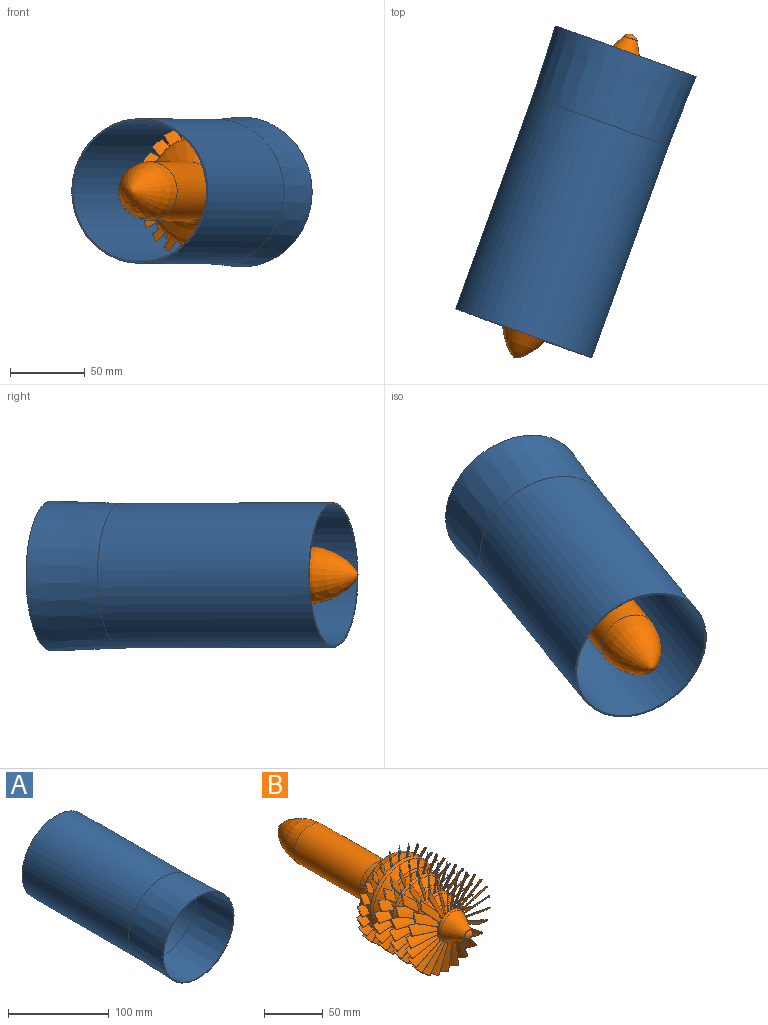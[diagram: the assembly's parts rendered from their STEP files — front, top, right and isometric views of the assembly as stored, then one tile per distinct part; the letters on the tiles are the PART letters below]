
ASSEMBLY  parts=2 mates=1
PART A: 6 faces, bbox 100x200x100 mm
  f0: cone r=50mm half-angle=2deg, axis (0,-1,0), area 15443.1mm2, adj f1,f5
  f1: plane 100x100mm, normal (0,-1,0), area 311mm2, adj f0,f2
  f2: cone r=49mm half-angle=2deg, axis (0,-1,0), area 15128.8mm2, adj f1,f3
  f3: cylinder r=47.25mm len=150mm, axis (0,-1,0), area 44535.8mm2, adj f2,f4
  f4: plane 96.51x96.51mm, normal (0,1,0), area 300mm2, adj f3,f5
  f5: cylinder r=48.25mm len=150mm, axis (0,-1,0), area 45478.3mm2, adj f0,f4
PART B: 370 faces, bbox 95.2x229.3x95.1 mm
  f0: cylinder r=22.77mm len=10.61mm, axis (0,-1,0), area 35.7mm2, adj f178,f180,f367,f369
  f1: cylinder r=22.77mm len=11.53mm, axis (0,-1,0), area 35.7mm2, adj f181,f183,f367,f369
  f2: cylinder r=22.77mm len=11.73mm, axis (0,-1,0), area 30.5mm2, adj f184,f186,f367,f368,f369
  f3: cylinder r=22.77mm len=11.19mm, axis (0,-1,0), area 35.7mm2, adj f187,f189,f367,f369
  f4: cylinder r=22.77mm len=9.95mm, axis (0,-1,0), area 35.7mm2, adj f190,f192,f367,f369
  f5: cylinder r=22.77mm len=8.53mm, axis (0,-1,0), area 35.7mm2, adj f193,f195,f367,f369
  f6: cylinder r=22.77mm len=10.27mm, axis (0,-1,0), area 35.7mm2, adj f196,f198,f367,f369
  f7: cylinder r=22.77mm len=11.37mm, axis (0,-1,0), area 35.7mm2, adj f199,f201,f367,f369
  f8: cylinder r=22.77mm len=11.75mm, axis (0,-1,0), area 35.7mm2, adj f202,f204,f367,f369
  f9: cylinder r=22.77mm len=11.39mm, axis (0,-1,0), area 35.7mm2, adj f205,f207,f367,f369
  f10: cylinder r=22.77mm len=10.32mm, axis (0,-1,0), area 35.7mm2, adj f208,f210,f367,f369
  f11: cylinder r=22.77mm len=8.6mm, axis (0,-1,0), area 35.7mm2, adj f142,f209,f367,f369
  f12: cylinder r=22.77mm len=9.9mm, axis (0,-1,0), area 35.7mm2, adj f139,f141,f367,f369
  f13: cylinder r=22.77mm len=11.16mm, axis (0,-1,0), area 35.7mm2, adj f138,f147,f367,f369
  f14: cylinder r=22.77mm len=11.72mm, axis (0,-1,0), area 30.5mm2, adj f148,f150,f367,f369
  f15: cylinder r=22.77mm len=11.55mm, axis (0,-1,0), area 35.7mm2, adj f145,f151,f367,f369
  f16: cylinder r=22.77mm len=10.65mm, axis (0,-1,0), area 35.7mm2, adj f144,f159,f367,f369
  f17: cylinder r=22.77mm len=9.08mm, axis (0,-1,0), area 35.7mm2, adj f160,f162,f367,f369
  f18: cylinder r=22.77mm len=9.48mm, axis (0,-1,0), area 35.7mm2, adj f157,f163,f367,f369
  f19: cylinder r=22.77mm len=10.91mm, axis (0,-1,0), area 35.7mm2, adj f154,f156,f367,f369
  f20: cylinder r=22.77mm len=11.65mm, axis (0,-1,0), area 35.7mm2, adj f153,f166,f367,f369
  f21: cylinder r=22.77mm len=11.66mm, axis (0,-1,0), area 35.7mm2, adj f165,f169,f367,f369
  f22: cylinder r=22.77mm len=10.94mm, axis (0,-1,0), area 35.7mm2, adj f168,f172,f367,f369
  f23: cylinder r=22.77mm len=9.53mm, axis (0,-1,0), area 35.7mm2, adj f171,f175,f367,f369
  f24: cylinder r=30.05mm len=12.66mm, axis (0,-1,0), area 48mm2, adj f328,f330,f365,f366
  f25: cylinder r=30.05mm len=13.49mm, axis (0,-1,0), area 48mm2, adj f331,f333,f365,f366
  f26: cylinder r=30.05mm len=13.47mm, axis (0,-1,0), area 48mm2, adj f334,f336,f365,f366
  f27: cylinder r=30.05mm len=12.6mm, axis (0,-1,0), area 48mm2, adj f337,f339,f365,f366
  f28: cylinder r=30.05mm len=10.95mm, axis (0,-1,0), area 48mm2, adj f340,f342,f365,f366
  f29: cylinder r=30.05mm len=10.52mm, axis (0,-1,0), area 48mm2, adj f343,f345,f365,f366
  f30: cylinder r=30.05mm len=12.33mm, axis (0,-1,0), area 48mm2, adj f346,f348,f365,f366
  f31: cylinder r=30.05mm len=13.36mm, axis (0,-1,0), area 48mm2, adj f349,f351,f365,f366
  f32: cylinder r=30.05mm len=13.55mm, axis (0,-1,0), area 48mm2, adj f352,f354,f365,f366
  f33: cylinder r=30.05mm len=12.9mm, axis (0,-1,0), area 48mm2, adj f355,f357,f365,f366
  f34: cylinder r=30.05mm len=11.43mm, axis (0,-1,0), area 48mm2, adj f358,f360,f365,f366
  f35: cylinder r=30.05mm len=9.96mm, axis (0,-1,0), area 48mm2, adj f291,f359,f365,f366
  f36: cylinder r=30.05mm len=11.94mm, axis (0,-1,0), area 48mm2, adj f288,f292,f365,f366
  f37: cylinder r=30.05mm len=13.18mm, axis (0,-1,0), area 48mm2, adj f289,f297,f365,f366
  f38: cylinder r=30.05mm len=13.59mm, axis (0,-1,0), area 48mm2, adj f298,f300,f365,f366
  f39: cylinder r=30.05mm len=13.14mm, axis (0,-1,0), area 48mm2, adj f294,f301,f365,f366
  f40: cylinder r=30.05mm len=11.87mm, axis (0,-1,0), area 48mm2, adj f295,f309,f365,f366
  f41: cylinder r=30.05mm len=9.85mm, axis (0,-1,0), area 48mm2, adj f310,f312,f365,f366
  f42: cylinder r=30.05mm len=11.51mm, axis (0,-1,0), area 48mm2, adj f306,f313,f365,f366
  f43: cylinder r=30.05mm len=12.95mm, axis (0,-1,0), area 48mm2, adj f303,f307,f365,f366
  f44: cylinder r=30.05mm len=13.56mm, axis (0,-1,0), area 48mm2, adj f304,f316,f365,f366
  f45: cylinder r=30.05mm len=13.33mm, axis (0,-1,0), area 48mm2, adj f315,f319,f365,f366
  f46: cylinder r=30.05mm len=12.26mm, axis (0,-1,0), area 48mm2, adj f318,f322,f365,f366
  f47: cylinder r=30.05mm len=10.42mm, axis (0,-1,0), area 48mm2, adj f321,f325,f365,f366
  f48: cylinder r=30.05mm len=11.04mm, axis (0,-1,0), area 48mm2, adj f324,f327,f365,f366
  f49: cylinder r=37.33mm len=74.66mm, axis (0,-1,0), area 1745mm2, adj f50,f59,f213,f214,f216,f217,f219,f220
  f50: cylinder r=37.33mm len=6.36mm, axis (0,-1,0), area 18.9mm2, adj f49,f258,f364
  f51: cylinder r=22.77mm len=9.02mm, axis (0,-1,0), area 35.7mm2, adj f174,f177,f367,f369
  f52: cylinder r=15.49mm len=30.98mm, axis (0,-1,0), area 575mm2, adj f53,f63,f64,f66,f67,f69,f70,f72
  f53: cylinder r=15.49mm len=3.79mm, axis (0,-1,0), area 6.1mm2, adj f52,f96,f100,f362
  f54: cone r=22.77mm half-angle=36.1deg, axis (0,1,0), area 1095.6mm2, adj f362,f369
  f55: cone r=15.49mm half-angle=28.8deg, axis (0,1,0), area 1297.2mm2, adj f56,f363
  f56: sphere r=5.39mm, area 94.4mm2, adj f55
  f57: revolved ~39.03x38.98mm, area 3530.5mm2, adj f58
  f58: cylinder r=19.54mm len=78.57mm, axis (0,-1,0), area 9647.2mm2, adj f57,f59
  f59: revolved ~74.66x74.66mm, area 5313.1mm2, adj f49,f58
  f60: cone r=37.33mm half-angle=36.1deg, axis (0,1,0), area 1929.3mm2, adj f364,f365
  f61: cone r=30.05mm half-angle=36.1deg, axis (0,1,0), area 1512.5mm2, adj f366,f367
  f62: cone r=49mm half-angle=2deg, axis (0,-1,0), area 4.1mm2, adj f63,f64
  f63: extruded ~33.09x14.94mm, area 321.3mm2, adj f52,f62,f64,f362
  f64: extruded ~33.12x14.9mm, area 321.3mm2, adj f52,f62,f63,f362
  f65: cone r=49mm half-angle=2deg, axis (0,-1,0), area 4.1mm2, adj f66,f67
  f66: extruded ~31.77x21.82mm, area 321.3mm2, adj f52,f65,f67,f362
  f67: extruded ~31.78x21.8mm, area 321.3mm2, adj f52,f65,f66,f362
  f68: cone r=49mm half-angle=2deg, axis (0,-1,0), area 4.1mm2, adj f69,f70
  f69: extruded ~28.45x27.33mm, area 321.3mm2, adj f52,f68,f70,f362
  f70: extruded ~28.45x27.32mm, area 321.3mm2, adj f52,f68,f69,f362
  f71: cone r=49mm half-angle=2deg, axis (0,-1,0), area 4.1mm2, adj f72,f73
  f72: extruded ~31.12x23.34mm, area 321.3mm2, adj f52,f71,f73,f362
  f73: extruded ~31.13x23.32mm, area 321.3mm2, adj f52,f71,f72,f362
  f74: cone r=49mm half-angle=2deg, axis (0,-1,0), area 4.1mm2, adj f75,f76
  f75: extruded ~32.96x16.76mm, area 321.3mm2, adj f52,f74,f76,f362
  f76: extruded ~32.98x16.73mm, area 321.3mm2, adj f52,f74,f75,f362
  f77: cone r=49mm half-angle=2deg, axis (0,-1,0), area 4.1mm2, adj f78,f79
  f78: extruded ~32.72x9.13mm, area 321.3mm2, adj f52,f77,f79,f362
  f79: extruded ~32.76x9.09mm, area 321.3mm2, adj f52,f77,f78,f362
  f80: cone r=49mm half-angle=2deg, axis (0,-1,0), area 4.1mm2, adj f81,f82
  f81: extruded ~33.1x13.05mm, area 321.3mm2, adj f52,f80,f82,f362
  f82: extruded ~33.13x13.01mm, area 321.3mm2, adj f52,f80,f81,f362
  f83: cone r=49mm half-angle=2deg, axis (0,-1,0), area 4.1mm2, adj f84,f85
  f84: extruded ~32.29x20.21mm, area 321.3mm2, adj f52,f83,f85,f362
  f85: extruded ~32.31x20.19mm, area 321.3mm2, adj f52,f83,f84,f362
  f86: cone r=49mm half-angle=2deg, axis (0,-1,0), area 4.1mm2, adj f87,f88
  f87: extruded ~29.45x26.1mm, area 321.3mm2, adj f52,f86,f88,f362
  f88: extruded ~29.46x26.09mm, area 321.3mm2, adj f52,f86,f87,f362
  f89: cone r=49mm half-angle=2deg, axis (0,-1,0), area 4.1mm2, adj f90,f91
  f90: extruded ~30.35x24.77mm, area 321.3mm2, adj f52,f89,f91,f362
  f91: extruded ~30.35x24.76mm, area 321.3mm2, adj f52,f89,f90,f362
  f92: cone r=49mm half-angle=2deg, axis (0,-1,0), area 4.1mm2, adj f93,f94
  f93: extruded ~32.69x18.52mm, area 321.3mm2, adj f52,f92,f94,f362
  f94: extruded ~32.71x18.5mm, area 321.3mm2, adj f52,f92,f93,f362
  f95: cone r=49mm half-angle=2deg, axis (0,-1,0), area 4.1mm2, adj f96,f97
  f96: extruded ~32.97x11.11mm, area 321.7mm2, adj f52,f53,f95,f97,f362
  f97: extruded ~33.01x11.07mm, area 321.3mm2, adj f52,f95,f96,f362
  f98: cone r=49mm half-angle=2deg, axis (0,-1,0), area 4.1mm2, adj f99,f100
  f99: extruded ~32.98x11.11mm, area 321.3mm2, adj f52,f98,f100,f362
  f100: extruded ~33.01x11.07mm, area 321.3mm2, adj f52,f53,f98,f99,f362
  f101: cone r=49mm half-angle=2deg, axis (0,-1,0), area 4.1mm2, adj f102,f103
  f102: extruded ~32.71x18.5mm, area 321.3mm2, adj f52,f101,f103,f362
  f103: extruded ~32.69x18.52mm, area 321.3mm2, adj f52,f101,f102,f362
  f104: cone r=49mm half-angle=2deg, axis (0,-1,0), area 4.1mm2, adj f105,f106
  f105: extruded ~30.35x24.76mm, area 321.3mm2, adj f52,f104,f106,f362
  f106: extruded ~30.35x24.77mm, area 321.3mm2, adj f52,f104,f105,f362
  f107: cone r=49mm half-angle=2deg, axis (0,-1,0), area 4.1mm2, adj f108,f109
  f108: extruded ~29.46x26.09mm, area 321.3mm2, adj f52,f107,f109,f362
  f109: extruded ~29.45x26.1mm, area 321.3mm2, adj f52,f107,f108,f362
  f110: cone r=49mm half-angle=2deg, axis (0,-1,0), area 4.1mm2, adj f111,f112
  f111: extruded ~32.31x20.19mm, area 321.3mm2, adj f52,f110,f112,f362
  f112: extruded ~32.29x20.21mm, area 321.3mm2, adj f52,f110,f111,f362
  f113: cone r=49mm half-angle=2deg, axis (0,-1,0), area 4.1mm2, adj f114,f115
  f114: extruded ~33.13x13.01mm, area 321.3mm2, adj f52,f113,f115,f362
  f115: extruded ~33.1x13.05mm, area 321.3mm2, adj f52,f113,f114,f362
  f116: cone r=49mm half-angle=2deg, axis (0,-1,0), area 4.1mm2, adj f117,f118
  f117: extruded ~32.76x9.09mm, area 321.3mm2, adj f52,f116,f118,f362
  f118: extruded ~32.72x9.13mm, area 321.3mm2, adj f52,f116,f117,f362
  f119: cone r=49mm half-angle=2deg, axis (0,-1,0), area 4.1mm2, adj f120,f121
  f120: extruded ~32.98x16.73mm, area 321.3mm2, adj f52,f119,f121,f362
  f121: extruded ~32.96x16.76mm, area 321.3mm2, adj f52,f119,f120,f362
  f122: cone r=49mm half-angle=2deg, axis (0,-1,0), area 4.1mm2, adj f123,f124
  f123: extruded ~31.13x23.32mm, area 321.3mm2, adj f52,f122,f124,f362
  f124: extruded ~31.12x23.34mm, area 321.3mm2, adj f52,f122,f123,f362
  f125: cone r=49mm half-angle=2deg, axis (0,-1,0), area 4.1mm2, adj f126,f127
  f126: extruded ~28.45x27.32mm, area 321.3mm2, adj f52,f125,f127,f362
  f127: extruded ~28.45x27.33mm, area 321.3mm2, adj f52,f125,f126,f362
  f128: cone r=49mm half-angle=2deg, axis (0,-1,0), area 4.1mm2, adj f129,f130
  f129: extruded ~31.78x21.8mm, area 321.3mm2, adj f52,f128,f130,f362
  f130: extruded ~31.77x21.82mm, area 321.3mm2, adj f52,f128,f129,f362
  f131: cone r=49mm half-angle=2deg, axis (0,-1,0), area 4.1mm2, adj f132,f133
  f132: extruded ~33.12x14.9mm, area 321.3mm2, adj f52,f131,f133,f362
  f133: extruded ~33.09x14.94mm, area 321.3mm2, adj f52,f131,f132,f362
  f134: extruded ~32.34x7.12mm, area 321.3mm2, adj f52,f135,f136,f362
  f135: extruded ~32.38x7.12mm, area 321.3mm2, adj f52,f134,f136,f362
  f136: cone r=49mm half-angle=2deg, axis (0,-1,0), area 4.1mm2, adj f134,f135
  f137: cone r=49mm half-angle=2deg, axis (0,-1,0), area 4.1mm2, adj f138,f139
  f138: extruded ~24.97x16.62mm, area 240.7mm2, adj f13,f137,f139,f367,f369
  f139: extruded ~25x16.6mm, area 240.8mm2, adj f12,f137,f138,f367,f369
  f140: cone r=49mm half-angle=2deg, axis (0,-1,0), area 4.1mm2, adj f141,f142
  f141: extruded ~23.27x20.83mm, area 240.7mm2, adj f12,f140,f142,f367,f369
  f142: extruded ~23.28x20.82mm, area 240.8mm2, adj f11,f140,f141,f367,f369
  f143: cone r=49mm half-angle=2deg, axis (0,-1,0), area 4.1mm2, adj f144,f145
  f144: extruded ~25.23x14.4mm, area 240.7mm2, adj f16,f143,f145,f367,f369
  f145: extruded ~25.27x14.37mm, area 240.8mm2, adj f15,f143,f144,f367,f369
  f146: cone r=49mm half-angle=2deg, axis (0,-1,0), area 4.1mm2, adj f147,f148
  f147: extruded ~25.15x11.34mm, area 240.8mm2, adj f13,f146,f148,f367,f369
  f148: extruded ~25.11x11.37mm, area 240.7mm2, adj f14,f146,f147,f367,f369
  f149: cone r=49mm half-angle=2deg, axis (0,-1,0), area 4.1mm2, adj f150,f151
  f150: extruded ~24.71x8.75mm, area 240.8mm2, adj f14,f149,f151,f367,f369
  f151: extruded ~24.66x8.79mm, area 240.7mm2, adj f15,f149,f150,f367,f369
  f152: cone r=49mm half-angle=2deg, axis (0,-1,0), area 4.1mm2, adj f153,f154
  f153: extruded ~25.22x12.77mm, area 240.7mm2, adj f20,f152,f154,f367,f369
  f154: extruded ~25.26x12.73mm, area 240.8mm2, adj f19,f152,f153,f367,f369
  f155: cone r=49mm half-angle=2deg, axis (0,-1,0), area 4.1mm2, adj f156,f157
  f156: extruded ~24.69x17.78mm, area 240.7mm2, adj f19,f155,f157,f367,f369
  f157: extruded ~24.72x17.77mm, area 240.8mm2, adj f18,f155,f156,f367,f369
  f158: cone r=49mm half-angle=2deg, axis (0,-1,0), area 4.1mm2, adj f159,f160
  f159: extruded ~24.24x19.09mm, area 240.8mm2, adj f16,f158,f160,f367,f369
  f160: extruded ~24.22x19.1mm, area 240.7mm2, adj f17,f158,f159,f367,f369
  f161: cone r=49mm half-angle=2deg, axis (0,-1,0), area 4.1mm2, adj f162,f163
  f162: extruded ~22.62x21.68mm, area 240.8mm2, adj f17,f161,f163,f367,f369
  f163: extruded ~22.61x21.68mm, area 240.7mm2, adj f18,f161,f162,f367,f369
  f164: cone r=49mm half-angle=2deg, axis (0,-1,0), area 4.1mm2, adj f165,f166
  f165: extruded ~24.27x7.29mm, area 240.7mm2, adj f21,f164,f166,f367,f369
  f166: extruded ~24.32x7.24mm, area 240.8mm2, adj f20,f164,f165,f367,f369
  f167: cone r=49mm half-angle=2deg, axis (0,-1,0), area 4.1mm2, adj f168,f169
  f168: extruded ~25.24x13.07mm, area 240.7mm2, adj f22,f167,f169,f367,f369
  f169: extruded ~25.28x13.04mm, area 240.8mm2, adj f21,f167,f168,f367,f369
  f170: cone r=49mm half-angle=2deg, axis (0,-1,0), area 4.1mm2, adj f171,f172
  f171: extruded ~24.62x18.03mm, area 240.7mm2, adj f23,f170,f172,f367,f369
  f172: extruded ~24.64x18.02mm, area 240.8mm2, adj f22,f170,f171,f367,f369
  f173: cone r=49mm half-angle=2deg, axis (0,-1,0), area 4.1mm2, adj f174,f175
  f174: extruded ~22.45x21.86mm, area 240.7mm2, adj f51,f173,f175,f367,f369
  f175: extruded ~22.46x21.86mm, area 240.8mm2, adj f23,f173,f174,f367,f369
  f176: cone r=49mm half-angle=2deg, axis (0,-1,0), area 4.1mm2, adj f177,f178
  f177: extruded ~24.33x18.86mm, area 240.8mm2, adj f51,f176,f178,f367,f369
  f178: extruded ~24.31x18.87mm, area 240.7mm2, adj f0,f176,f177,f367,f369
  f179: cone r=49mm half-angle=2deg, axis (0,-1,0), area 4.1mm2, adj f180,f181
  f180: extruded ~25.28x14.08mm, area 240.8mm2, adj f0,f179,f181,f367,f369
  f181: extruded ~25.24x14.11mm, area 240.7mm2, adj f1,f179,f180,f367,f369
  f182: cone r=49mm half-angle=2deg, axis (0,-1,0), area 4.1mm2, adj f183,f184
  f183: extruded ~24.63x8.42mm, area 240.8mm2, adj f1,f182,f184,f367,f369
  f184: extruded ~24.58x8.46mm, area 240.7mm2, adj f2,f182,f183,f367,f369
  f185: cone r=49mm half-angle=2deg, axis (0,-1,0), area 4.1mm2, adj f186,f187
  f186: extruded ~25.19x11.65mm, area 240.8mm2, adj f2,f185,f187,f368,f369
  f187: extruded ~25.14x11.69mm, area 240.7mm2, adj f3,f185,f186,f367,f369
  f188: cone r=49mm half-angle=2deg, axis (0,-1,0), area 4.1mm2, adj f189,f190
  f189: extruded ~24.95x16.87mm, area 240.8mm2, adj f3,f188,f190,f367,f369
  f190: extruded ~24.92x16.89mm, area 240.7mm2, adj f4,f188,f189,f367,f369
  f191: cone r=49mm half-angle=2deg, axis (0,-1,0), area 4.1mm2, adj f192,f193
  f192: extruded ~23.14x21.02mm, area 240.8mm2, adj f4,f191,f193,f367,f369
  f193: extruded ~23.13x21.02mm, area 240.7mm2, adj f5,f191,f192,f367,f369
  f194: cone r=49mm half-angle=2deg, axis (0,-1,0), area 4.1mm2, adj f195,f196
  f195: extruded ~23.85x19.88mm, area 240.8mm2, adj f5,f194,f196,f367,f369
  f196: extruded ~23.84x19.89mm, area 240.7mm2, adj f6,f194,f195,f367,f369
  f197: cone r=49mm half-angle=2deg, axis (0,-1,0), area 4.1mm2, adj f198,f199
  f198: extruded ~25.19x15.37mm, area 240.8mm2, adj f6,f197,f199,f367,f369
  f199: extruded ~25.16x15.4mm, area 240.7mm2, adj f7,f197,f198,f367,f369
  f200: cone r=49mm half-angle=2deg, axis (0,-1,0), area 4.1mm2, adj f201,f202
  f201: extruded ~24.94x9.9mm, area 240.8mm2, adj f7,f200,f202,f367,f369
  f202: extruded ~24.89x9.94mm, area 240.7mm2, adj f8,f200,f201,f367,f369
  f203: cone r=49mm half-angle=2deg, axis (0,-1,0), area 4.1mm2, adj f204,f205
  f204: extruded ~25x10.22mm, area 240.8mm2, adj f8,f203,f205,f367,f369
  f205: extruded ~24.95x10.26mm, area 240.7mm2, adj f9,f203,f204,f367,f369
  f206: cone r=49mm half-angle=2deg, axis (0,-1,0), area 4.1mm2, adj f207,f208
  f207: extruded ~25.16x15.65mm, area 240.8mm2, adj f9,f206,f208,f367,f369
  f208: extruded ~25.12x15.67mm, area 240.7mm2, adj f10,f206,f207,f367,f369
  f209: extruded ~23.72x20.1mm, area 240.7mm2, adj f11,f210,f211,f367,f369
  f210: extruded ~23.73x20.1mm, area 240.8mm2, adj f10,f209,f211,f367,f369
  f211: cone r=49mm half-angle=2deg, axis (0,-1,0), area 4.1mm2, adj f209,f210
  f212: cylinder r=47.25mm len=7.07mm, axis (0,-1,0), area 4.1mm2, adj f213,f214
  f213: extruded ~10.75x9.4mm, area 90.5mm2, adj f49,f212,f214,f364
  f214: extruded ~10.77x9.44mm, area 89.7mm2, adj f49,f212,f213,f364
  f215: cylinder r=47.25mm len=7.07mm, axis (0,-1,0), area 4.1mm2, adj f216,f217
  f216: extruded ~11.44x10.76mm, area 90.5mm2, adj f49,f215,f217,f364
  f217: extruded ~11.47x10.8mm, area 89.7mm2, adj f49,f215,f216,f364
  f218: cylinder r=47.25mm len=7.12mm, axis (0,-1,0), area 4.1mm2, adj f219,f220
  f219: extruded ~9.38x7.45mm, area 90.5mm2, adj f49,f218,f220,f364
  f220: extruded ~9.39x7.49mm, area 89.7mm2, adj f49,f218,f219,f364
  f221: cylinder r=47.25mm len=7.07mm, axis (0,-1,0), area 4.1mm2, adj f222,f223
  f222: extruded ~10.37x8.81mm, area 90.5mm2, adj f49,f221,f223,f364
  f223: extruded ~10.38x8.85mm, area 89.7mm2, adj f49,f221,f222,f364
  f224: cylinder r=47.25mm len=7.07mm, axis (0,-1,0), area 4.1mm2, adj f225,f226
  f225: extruded ~11.29x10.38mm, area 90.5mm2, adj f49,f224,f226,f364
  f226: extruded ~11.31x10.42mm, area 89.7mm2, adj f49,f224,f225,f364
  f227: cylinder r=47.25mm len=7.09mm, axis (0,-1,0), area 4.1mm2, adj f228,f229
  f228: extruded ~9.79x7.98mm, area 90.5mm2, adj f49,f227,f229,f364
  f229: extruded ~9.79x8.03mm, area 89.7mm2, adj f49,f227,f228,f364
  f230: cylinder r=47.25mm len=7.07mm, axis (0,-1,0), area 4.1mm2, adj f231,f232
  f231: extruded ~10.99x9.8mm, area 90.5mm2, adj f49,f230,f232,f364
  f232: extruded ~11.01x9.84mm, area 89.7mm2, adj f49,f230,f231,f364
  f233: cylinder r=47.25mm len=7.07mm, axis (0,-1,0), area 4.1mm2, adj f234,f235
  f234: extruded ~11.51x11.3mm, area 90.5mm2, adj f49,f233,f235,f364
  f235: extruded ~11.54x11.33mm, area 89.7mm2, adj f49,f233,f234,f364
  f236: cylinder r=47.25mm len=7.07mm, axis (0,-1,0), area 4.1mm2, adj f237,f238
  f237: extruded ~11.5x11mm, area 90.5mm2, adj f49,f236,f238,f364
  f238: extruded ~11.53x11.04mm, area 89.7mm2, adj f49,f236,f237,f364
  f239: cylinder r=47.25mm len=7.07mm, axis (0,-1,0), area 4.1mm2, adj f240,f241
  f240: extruded ~10.04x8.37mm, area 89.7mm2, adj f49,f239,f241,f364
  f241: extruded ~10.03x8.32mm, area 90.5mm2, adj f49,f239,f240,f364
  f242: cylinder r=47.25mm len=7.07mm, axis (0,-1,0), area 4.1mm2, adj f243,f244
  f243: extruded ~11.15x10.09mm, area 89.7mm2, adj f49,f242,f244,f364
  f244: extruded ~11.13x10.04mm, area 90.5mm2, adj f49,f242,f243,f364
  f245: cylinder r=47.25mm len=7.07mm, axis (0,-1,0), area 4.1mm2, adj f246,f247
  f246: extruded ~11.55x11.17mm, area 89.7mm2, adj f49,f245,f247,f364
  f247: extruded ~11.52x11.13mm, area 90.5mm2, adj f49,f245,f246,f364
  f248: cylinder r=47.25mm len=7.07mm, axis (0,-1,0), area 4.1mm2, adj f249,f250
  f249: extruded ~11.55x11.23mm, area 89.7mm2, adj f49,f248,f250,f364
  f250: extruded ~11.52x11.19mm, area 90.5mm2, adj f49,f248,f249,f364
  f251: cylinder r=47.25mm len=7.07mm, axis (0,-1,0), area 4.1mm2, adj f252,f253
  f252: extruded ~11.19x10.16mm, area 90.5mm2, adj f49,f251,f253,f364
  f253: extruded ~11.21x10.2mm, area 89.7mm2, adj f49,f251,f252,f364
  f254: cylinder r=47.25mm len=7.07mm, axis (0,-1,0), area 4.1mm2, adj f255,f256
  f255: extruded ~10.15x8.49mm, area 90.5mm2, adj f49,f254,f256,f364
  f256: extruded ~10.16x8.54mm, area 89.7mm2, adj f49,f254,f255,f364
  f257: cylinder r=47.25mm len=7.1mm, axis (0,-1,0), area 4.1mm2, adj f258,f259
  f258: extruded ~9.66x7.81mm, area 90.4mm2, adj f49,f50,f257,f259,f364
  f259: extruded ~9.66x7.85mm, area 89.7mm2, adj f49,f257,f258,f364
  f260: cylinder r=47.25mm len=7.07mm, axis (0,-1,0), area 4.1mm2, adj f261,f262
  f261: extruded ~10.92x9.67mm, area 90.5mm2, adj f49,f260,f262,f364
  f262: extruded ~10.93x9.71mm, area 89.7mm2, adj f49,f260,f261,f364
  f263: cylinder r=47.25mm len=7.07mm, axis (0,-1,0), area 4.1mm2, adj f264,f265
  f264: extruded ~11.49x10.92mm, area 90.5mm2, adj f49,f263,f265,f364
  f265: extruded ~11.52x10.96mm, area 89.7mm2, adj f49,f263,f264,f364
  f266: cylinder r=47.25mm len=7.07mm, axis (0,-1,0), area 4.1mm2, adj f267,f268
  f267: extruded ~11.49x11.34mm, area 90.5mm2, adj f49,f266,f268,f364
  f268: extruded ~11.52x11.38mm, area 89.7mm2, adj f49,f266,f267,f364
  f269: cylinder r=47.25mm len=7.07mm, axis (0,-1,0), area 4.1mm2, adj f270,f271
  f270: extruded ~11.34x10.48mm, area 90.5mm2, adj f49,f269,f271,f364
  f271: extruded ~11.36x10.52mm, area 89.7mm2, adj f49,f269,f270,f364
  f272: cylinder r=47.25mm len=7.07mm, axis (0,-1,0), area 4.1mm2, adj f273,f274
  f273: extruded ~10.47x8.96mm, area 90.5mm2, adj f49,f272,f274,f364
  f274: extruded ~10.48x9.01mm, area 89.7mm2, adj f49,f272,f273,f364
  f275: cylinder r=47.25mm len=7.13mm, axis (0,-1,0), area 4.1mm2, adj f276,f277
  f276: extruded ~9.24x7.26mm, area 90.5mm2, adj f49,f275,f277,f364
  f277: extruded ~9.25x7.31mm, area 89.7mm2, adj f49,f275,f276,f364
  f278: cylinder r=47.25mm len=7.07mm, axis (0,-1,0), area 4.1mm2, adj f279,f280
  f279: extruded ~10.66x9.26mm, area 90.5mm2, adj f49,f278,f280,f364
  f280: extruded ~10.68x9.3mm, area 89.7mm2, adj f49,f278,f279,f364
  f281: cylinder r=47.25mm len=7.07mm, axis (0,-1,0), area 4.1mm2, adj f282,f283
  f282: extruded ~11.41x10.67mm, area 90.5mm2, adj f49,f281,f283,f364
  f283: extruded ~11.44x10.71mm, area 89.7mm2, adj f49,f281,f282,f364
  f284: extruded ~11.48x11.45mm, area 89.7mm2, adj f49,f285,f286,f364
  f285: extruded ~11.45x11.42mm, area 90.5mm2, adj f49,f284,f286,f364
  f286: cylinder r=47.25mm len=7.07mm, axis (0,-1,0), area 4.1mm2, adj f284,f285
  f287: cylinder r=47.25mm len=7.07mm, axis (0,-1,0), area 4.1mm2, adj f288,f289
  f288: extruded ~17.86x12.44mm, area 162.9mm2, adj f36,f287,f289,f365,f366
  f289: extruded ~17.88x12.48mm, area 162.9mm2, adj f37,f287,f288,f365,f366
  f290: cylinder r=47.25mm len=7.07mm, axis (0,-1,0), area 4.1mm2, adj f291,f292
  f291: extruded ~17.49x15.24mm, area 162.9mm2, adj f35,f290,f292,f365,f366
  f292: extruded ~17.52x15.28mm, area 162.9mm2, adj f36,f290,f291,f365,f366
  f293: cylinder r=47.25mm len=7.07mm, axis (0,-1,0), area 4.1mm2, adj f294,f295
  f294: extruded ~17.87x12.79mm, area 162.9mm2, adj f39,f293,f295,f365,f366
  f295: extruded ~17.89x12.84mm, area 162.9mm2, adj f40,f293,f294,f365,f366
  f296: cylinder r=47.25mm len=7.09mm, axis (0,-1,0), area 4.1mm2, adj f297,f298
  f297: extruded ~17.1x8.86mm, area 162.9mm2, adj f37,f296,f298,f365,f366
  f298: extruded ~17.11x8.9mm, area 162.9mm2, adj f38,f296,f297,f365,f366
  f299: cylinder r=47.25mm len=7.07mm, axis (0,-1,0), area 4.1mm2, adj f300,f301
  f300: extruded ~17.24x9.29mm, area 162.9mm2, adj f38,f299,f301,f365,f366
  f301: extruded ~17.25x9.33mm, area 162.9mm2, adj f39,f299,f300,f365,f366
  f302: cylinder r=47.25mm len=7.07mm, axis (0,-1,0), area 4.1mm2, adj f303,f304
  f303: extruded ~17.39x9.81mm, area 162.9mm2, adj f43,f302,f304,f365,f366
  f304: extruded ~17.41x9.86mm, area 162.9mm2, adj f44,f302,f303,f365,f366
  f305: cylinder r=47.25mm len=7.07mm, axis (0,-1,0), area 4.1mm2, adj f306,f307
  f306: extruded ~17.87x13.22mm, area 162.9mm2, adj f42,f305,f307,f365,f366
  f307: extruded ~17.89x13.27mm, area 162.9mm2, adj f43,f305,f306,f365,f366
  f308: cylinder r=47.25mm len=7.07mm, axis (0,-1,0), area 4.1mm2, adj f309,f310
  f309: extruded ~17.38x15.5mm, area 162.9mm2, adj f40,f308,f310,f365,f366
  f310: extruded ~17.41x15.54mm, area 162.9mm2, adj f41,f308,f309,f365,f366
  f311: cylinder r=47.25mm len=7.07mm, axis (0,-1,0), area 4.1mm2, adj f312,f313
  f312: extruded ~17.22x15.8mm, area 162.9mm2, adj f41,f311,f313,f365,f366
  f313: extruded ~17.26x15.84mm, area 162.9mm2, adj f42,f311,f312,f365,f366
  f314: cylinder r=47.25mm len=7.11mm, axis (0,-1,0), area 4.1mm2, adj f315,f316
  f315: extruded ~16.92x8.36mm, area 162.9mm2, adj f45,f314,f316,f365,f366
  f316: extruded ~16.91x8.31mm, area 162.9mm2, adj f44,f314,f315,f365,f366
  f317: cylinder r=47.25mm len=7.07mm, axis (0,-1,0), area 4.1mm2, adj f318,f319
  f318: extruded ~17.84x12.03mm, area 162.9mm2, adj f46,f317,f319,f365,f366
  f319: extruded ~17.82x11.98mm, area 162.9mm2, adj f45,f317,f318,f365,f366
  f320: cylinder r=47.25mm len=7.07mm, axis (0,-1,0), area 4.1mm2, adj f321,f322
  f321: extruded ~17.64x14.95mm, area 162.9mm2, adj f47,f320,f322,f365,f366
  f322: extruded ~17.61x14.91mm, area 162.9mm2, adj f46,f320,f321,f365,f366
  f323: cylinder r=47.25mm len=7.07mm, axis (0,-1,0), area 4.1mm2, adj f324,f325
  f324: extruded ~16.92x16.33mm, area 162.9mm2, adj f48,f323,f325,f365,f366
  f325: extruded ~16.89x16.29mm, area 162.9mm2, adj f47,f323,f324,f365,f366
  f326: cylinder r=47.25mm len=7.07mm, axis (0,-1,0), area 4.1mm2, adj f327,f328
  f327: extruded ~17.81x13.95mm, area 162.9mm2, adj f48,f326,f328,f365,f366
  f328: extruded ~17.84x13.99mm, area 162.9mm2, adj f24,f326,f327,f365,f366
  f329: cylinder r=47.25mm len=7.07mm, axis (0,-1,0), area 4.1mm2, adj f330,f331
  f330: extruded ~17.62x10.73mm, area 162.9mm2, adj f24,f329,f331,f365,f366
  f331: extruded ~17.63x10.78mm, area 162.9mm2, adj f25,f329,f330,f365,f366
  f332: cylinder r=47.25mm len=7.13mm, axis (0,-1,0), area 4.1mm2, adj f333,f334
  f333: extruded ~16.51x7.3mm, area 162.9mm2, adj f25,f332,f334,f365,f366
  f334: extruded ~16.52x7.35mm, area 162.9mm2, adj f26,f332,f333,f365,f366
  f335: cylinder r=47.25mm len=7.07mm, axis (0,-1,0), area 4.1mm2, adj f336,f337
  f336: extruded ~17.7x11.13mm, area 162.9mm2, adj f26,f335,f337,f365,f366
  f337: extruded ~17.71x11.17mm, area 162.9mm2, adj f27,f335,f336,f365,f366
  f338: cylinder r=47.25mm len=7.07mm, axis (0,-1,0), area 4.1mm2, adj f339,f340
  f339: extruded ~17.77x14.26mm, area 162.9mm2, adj f27,f338,f340,f365,f366
  f340: extruded ~17.79x14.3mm, area 162.9mm2, adj f28,f338,f339,f365,f366
  f341: cylinder r=47.25mm len=7.07mm, axis (0,-1,0), area 4.1mm2, adj f342,f343
  f342: extruded ~16.72x16.49mm, area 162.9mm2, adj f28,f341,f343,f365,f366
  f343: extruded ~16.76x16.53mm, area 162.9mm2, adj f29,f341,f342,f365,f366
  f344: cylinder r=47.25mm len=7.07mm, axis (0,-1,0), area 4.1mm2, adj f345,f346
  f345: extruded ~17.69x14.62mm, area 162.9mm2, adj f29,f344,f346,f365,f366
  f346: extruded ~17.71x14.67mm, area 162.9mm2, adj f30,f344,f345,f365,f366
  f347: cylinder r=47.25mm len=7.07mm, axis (0,-1,0), area 4.1mm2, adj f348,f349
  f348: extruded ~17.77x11.61mm, area 162.9mm2, adj f30,f347,f349,f365,f366
  f349: extruded ~17.79x11.66mm, area 162.9mm2, adj f31,f347,f348,f365,f366
  f350: cylinder r=47.25mm len=7.12mm, axis (0,-1,0), area 4.1mm2, adj f351,f352
  f351: extruded ~16.74x7.86mm, area 162.9mm2, adj f31,f350,f352,f365,f366
  f352: extruded ~16.75x7.91mm, area 162.9mm2, adj f32,f350,f351,f365,f366
  f353: cylinder r=47.25mm len=7.07mm, axis (0,-1,0), area 4.1mm2, adj f354,f355
  f354: extruded ~17.5x10.23mm, area 162.9mm2, adj f32,f353,f355,f365,f366
  f355: extruded ~17.52x10.27mm, area 162.9mm2, adj f33,f353,f354,f365,f366
  f356: cylinder r=47.25mm len=7.07mm, axis (0,-1,0), area 4.1mm2, adj f357,f358
  f357: extruded ~17.85x13.55mm, area 162.9mm2, adj f33,f356,f358,f365,f366
  f358: extruded ~17.88x13.6mm, area 162.9mm2, adj f34,f356,f357,f365,f366
  f359: extruded ~17.12x16.06mm, area 162.9mm2, adj f35,f360,f361,f365,f366
  f360: extruded ~17.08x16.02mm, area 162.9mm2, adj f34,f359,f361,f365,f366
  f361: cylinder r=47.25mm len=7.07mm, axis (0,-1,0), area 4.1mm2, adj f359,f360
  f362: torus R=20.49mm, axis (0,-1,0), area 312.4mm2, adj f52,f53,f54,f63,f64,f66,f67,f69
  f363: torus R=10.49mm, axis (0,1,0), area 241.3mm2, adj f52,f55
  f364: torus R=32.33mm, axis (0,1,0), area 728.7mm2, adj f49,f50,f60,f213,f214,f216,f217,f219
  f365: torus R=35.05mm, axis (0,-1,0), area 600.2mm2, adj f24,f25,f26,f27,f28,f29,f30,f31
  f366: torus R=25.05mm, axis (0,1,0), area 584.8mm2, adj f24,f25,f26,f27,f28,f29,f30,f31
  f367: torus R=27.77mm, axis (0,-1,0), area 456.3mm2, adj f0,f1,f2,f3,f4,f5,f6,f7
  f368: torus R=27.77mm, axis (0,-1,0), area 0mm2, adj f2,f186,f367
  f369: torus R=17.77mm, axis (0,1,0), area 440.9mm2, adj f0,f1,f2,f3,f4,f5,f6,f7
PLACE A rot(axis=(-0.65,0.12,0.75),165.1deg) t=(134.73,358.23,-11.03)mm
PLACE B rot(axis=(-0.97,0.17,0.19),176.4deg) t=(135.29,359.77,-11.04)mm
MATE revolute B.f0 <-> A.f0  axis (-0.34,-0.94,0) through (141.53,377.04,-11.1)mm
